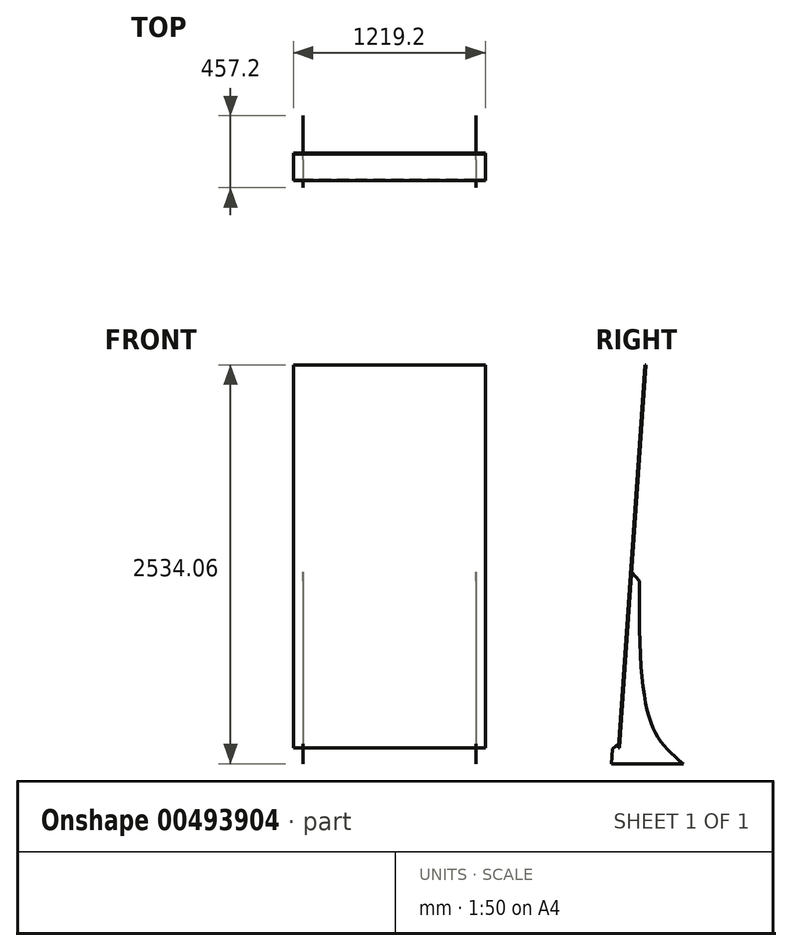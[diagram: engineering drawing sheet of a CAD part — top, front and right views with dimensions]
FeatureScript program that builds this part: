
annotation { "Feature Type Name" : "Feature", "Feature Type Description" : "" }
export const myFeature = defineFeature(function(context is Context, id is Id, definition is map)
    precondition{}
    {
        {
            var Q0;
            Q0=qCreatedBy(makeId("Right.planeOp"),FACE);
            var sketch = newSketch(context, id + "F0", { "sketchPlane" : qUnion([Q0])});
            skLineSegment(sketch, "E0", {"start": v(0, 0) * mm, "end": v(170.1, 2432.46) * mm});
            skLineSegment(sketch, "E1", {"start": v(0, 0) * mm, "end": v(0, 1268.46) * mm, "construction": true});
            skLineSegment(sketch, "E2", {"start": v(0, 0) * mm, "end": v(-6.59, 0.46) * mm});
            skLineSegment(sketch, "E3", {"start": v(-6.59, 0.46) * mm, "end": v(163.47, 2432.46) * mm});
            skLineSegment(sketch, "E4", {"start": v(170.1, 2432.46) * mm, "end": v(163.47, 2432.46) * mm});
            skLineSegment(sketch, "E5", {"start": v(-1524, 0.55) * mm, "end": v(-1524, 1524.55) * mm, "construction": true});
            skLineSegment(sketch, "E6", {"start": v(-1524, 1524.55) * mm, "end": v(92.08, 1411.55) * mm, "construction": true});
            skLineSegment(sketch, "E7", {"start": v(0, 0) * mm, "end": v(170.1, 0.46) * mm, "construction": true});
            skSolve(sketch);
        }
        {
            var Q0;
            Q0=qCreatedBy(makeId("Right.planeOp"),FACE);
            var sketch = newSketch(context, id + "F1", { "sketchPlane" : qUnion([Q0])});
            skLineSegment(sketch, "E8.bottom", {"start": v(0, 0) * mm, "end": v(-50.8, 0) * mm, "construction": true});
            skLineSegment(sketch, "E8.top", {"start": v(0, -101.6) * mm, "end": v(-50.8, -101.6) * mm, "construction": true});
            skLineSegment(sketch, "E8.left", {"start": v(0, 0) * mm, "end": v(0, -101.6) * mm, "construction": true});
            skLineSegment(sketch, "E8.right", {"start": v(-50.8, 0) * mm, "end": v(-50.8, -101.6) * mm, "construction": true});
            skLineSegment(sketch, "E9.bottom", {"start": v(0, 0) * mm, "end": v(406.4, 0) * mm, "construction": true});
            skLineSegment(sketch, "E9.top", {"start": v(0, -101.6) * mm, "end": v(406.4, -101.6) * mm, "construction": true});
            skLineSegment(sketch, "E9.right", {"start": v(406.4, 0) * mm, "end": v(406.4, -101.6) * mm, "construction": true});
            skLineSegment(sketch, "E10.0", {"start": v(0, 0) * mm, "end": v(170.1, 2432.46) * mm, "construction": true});
            skLineSegment(sketch, "E10.1", {"start": v(-6.59, 0.46) * mm, "end": v(163.47, 2432.46) * mm, "construction": true});
            skPoint(sketch, "E11.visualSharp", {"position": v(-50.8, -101.6) * mm});
            skLineSegment(sketch, "E12", {"start": v(-50.8, -101.6) * mm, "end": v(406.4, -101.6) * mm});
            skLineSegment(sketch, "E13", {"start": v(-43.18, -7.93) * mm, "end": v(-4.84, 25.4) * mm});
            skLineSegment(sketch, "E14", {"start": v(128.14, 1060.1) * mm, "end": v(78.15, 1117.6) * mm});
            skLineSegment(sketch, "E15", {"start": v(78.15, 1117.6) * mm, "end": v(0, 0) * mm});
            skLineSegment(sketch, "E16", {"start": v(-6.59, 0.46) * mm, "end": v(-4.84, 25.4) * mm});
            skLineSegment(sketch, "E17", {"start": v(-6.59, 0.46) * mm, "end": v(0, 0) * mm});
            skFitSpline(sketch, "E18", {"points": [v(128.14, 1060.1) * mm, v(406.4, -101.6) * mm], "startDerivative": vector(-22.76, -2625.47) * mm, "endDerivative": vector(654.1, -537.54) * mm});
            skPoint(sketch, "E19", {"position": v(-25.4, 0) * mm});
            skLineSegment(sketch, "E20", {"start": v(-50.8, -101.6) * mm, "end": v(-43.18, -7.93) * mm});
            skSolve(sketch);
        }
        {
            var Q0;
            Q0=makeQuery(id+"F0.imprint","IMPRINT",FACE,{"disambiguationData":[TD([[makeQuery(id+"F0.imprint","IMPRINT",EDGE,{"derivedFrom":sQuery(id+"F0.wireOp",EDGE,"E0")}),1.0]])]});
            extrude(context, id + "F2", {"entities" : qUnion([Q0]), "endBound" : BoundingType.SYMMETRIC, "depth" : 1219.2 * mm});
        }
        {
            var Q0;
            Q0 = qSketchRegion(id + "F1", true);
            extrude(context, id + "F3", {"entities" : qUnion([Q0]), "depth" : 548.64 * mm, "hasSecondDirection" : true, "secondDirectionOppositeDirection" : false, "secondDirectionDepth" : 548.64 * mm - 1 / 101.6 * mm});
        }
        {
            var Q0;
            Q0=makeQuery(id+"F3.opExtrude","SWEPT_BODY",BODY,{"disambiguationData":[OSD([sQuery(id+"F1.wireOp",EDGE,"E12"),sQuery(id+"F1.wireOp",EDGE,"67oeedWU-Vt2Q-a3r4-G2T7-g3kgQDFvsnQx"),sQuery(id+"F1.wireOp",EDGE,"E13"),sQuery(id+"F1.wireOp",EDGE,"2i0P1ZJF-hQgD-c8r3-r42B-r8zb1097eBHw"),sQuery(id+"F1.wireOp",EDGE,"E14"),sQuery(id+"F1.wireOp",EDGE,"E15"),sQuery(id+"F1.wireOp",EDGE,"E16"),sQuery(id+"F1.wireOp",EDGE,"E17")])]});
            var Q1;
            Q1=qCreatedBy(makeId("Right.planeOp"),FACE);
            mirror(context, id + "F4", {"operationType" : NewBodyOperationType.ADD, "entities" : qUnion([Q0]), "mirrorPlane" : qUnion([Q1])});
        }
    });
